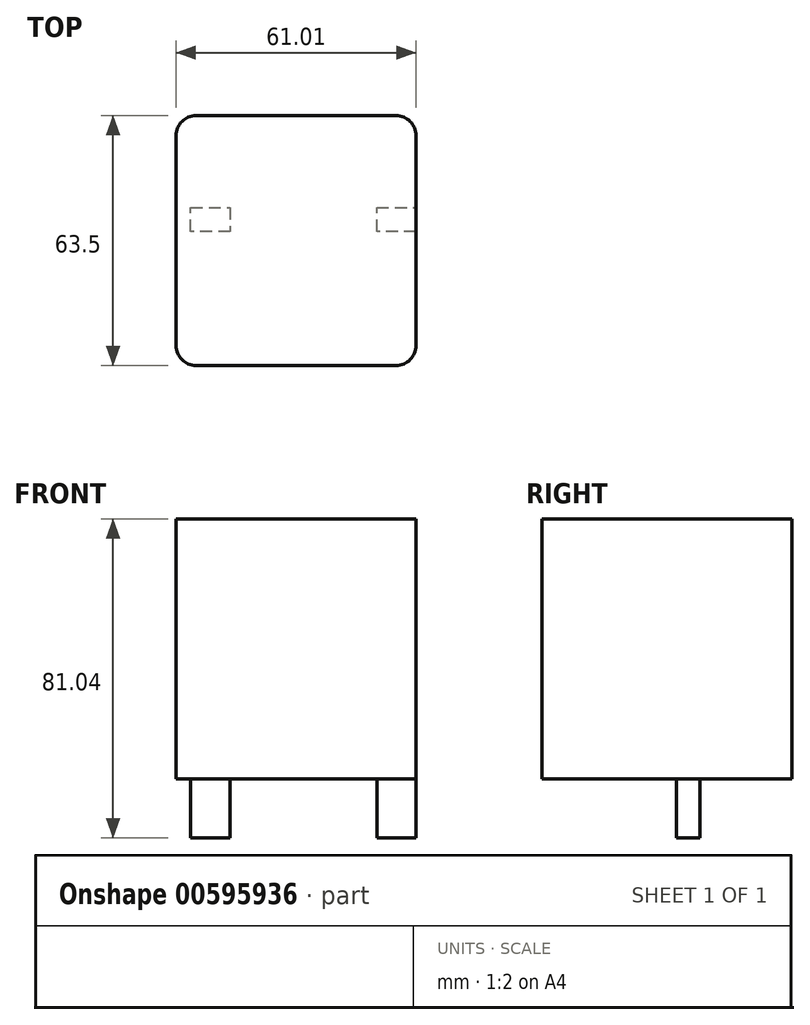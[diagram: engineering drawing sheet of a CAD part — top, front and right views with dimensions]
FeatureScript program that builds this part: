
annotation { "Feature Type Name" : "Feature", "Feature Type Description" : "" }
export const myFeature = defineFeature(function(context is Context, id is Id, definition is map)
    precondition{}
    {
        {
            var Q0;
            Q0=qCreatedBy(makeId("Right.planeOp"),FACE);
            var sketch = newSketch(context, id + "F0", { "sketchPlane" : qUnion([Q0])});
            skLineSegment(sketch, "E0", {"start": v(-37.4, 48.63) * mm, "end": v(26.1, 48.63) * mm});
            skLineSegment(sketch, "E1", {"start": v(26.1, 48.63) * mm, "end": v(26.1, -17.4) * mm});
            skLineSegment(sketch, "E2", {"start": v(26.1, -17.4) * mm, "end": v(-37.4, -17.4) * mm});
            skLineSegment(sketch, "E3", {"start": v(-37.4, -17.4) * mm, "end": v(-37.4, 48.63) * mm});
            skSolve(sketch);
        }
        {
            var Q0;
            Q0 = qSketchRegion(id + "F0", true);
            extrude(context, id + "F1", {"entities" : qUnion([Q0]), "depth" : 60.96 * mm, "offsetDistance" : 25.4 * mm});
        }
        {
            var Q0;
            Q0=makeQuery(id+"F1.opExtrude","CAP_EDGE",EDGE,{"disambiguationData":[OSD([sQuery(id+"F0.wireOp",EDGE,"E3")])],"isStart":false});
            var Q1;
            Q1=makeQuery(id+"F1.opExtrude","CAP_EDGE",EDGE,{"disambiguationData":[OSD([sQuery(id+"F0.wireOp",EDGE,"E1")])],"isStart":false});
            var Q2;
            Q2=makeQuery(id+"F1.opExtrude","CAP_EDGE",EDGE,{"disambiguationData":[OSD([sQuery(id+"F0.wireOp",EDGE,"E3")])],"isStart":true});
            var Q3;
            Q3=makeQuery(id+"F1.opExtrude","CAP_EDGE",EDGE,{"disambiguationData":[OSD([sQuery(id+"F0.wireOp",EDGE,"E1")])],"isStart":true});
            fillet(context, id + "F2", {"entities" : qUnion([Q0, Q1, Q2, Q3]), "radius" : 5.08 * mm, "tangentPropagation" : true, "allowEdgeOverflow" : false});
        }
        {
            var Q0;
            Q0=makeQuery(id+"F1.opExtrude","SWEPT_FACE",FACE,{"disambiguationData":[OSD([sQuery(id+"F0.wireOp",EDGE,"E2")])]});
            var sketch = newSketch(context, id + "F3", { "sketchPlane" : qUnion([Q0])});
            skLineSegment(sketch, "E4", {"start": v(30.48, 37.4) * mm, "end": v(30.48, -26.1) * mm, "construction": true});
            skLineSegment(sketch, "E5", {"start": v(0, 5.65) * mm, "end": v(60.96, 5.65) * mm, "construction": true});
            skPoint(sketch, "E6", {"position": v(30.48, 5.65) * mm});
            skLineSegment(sketch, "E7", {"start": v(3.74, 3.31) * mm, "end": v(3.74, -2.69) * mm});
            skLineSegment(sketch, "E8", {"start": v(3.74, -2.69) * mm, "end": v(13.74, -2.69) * mm});
            skLineSegment(sketch, "E9", {"start": v(13.74, -2.69) * mm, "end": v(13.74, 3.31) * mm});
            skLineSegment(sketch, "E10", {"start": v(13.74, 3.31) * mm, "end": v(3.74, 3.31) * mm});
            skLineSegment(sketch, "E11", {"start": v(51, 3.31) * mm, "end": v(51, -2.69) * mm});
            skLineSegment(sketch, "E12", {"start": v(51, -2.69) * mm, "end": v(61, -2.69) * mm});
            skLineSegment(sketch, "E13", {"start": v(61, -2.69) * mm, "end": v(61, 3.31) * mm});
            skLineSegment(sketch, "E14", {"start": v(61, 3.31) * mm, "end": v(51, 3.31) * mm});
            skSolve(sketch);
        }
        {
            var Q0;
            Q0 = qSketchRegion(id + "F3", true);
            extrude(context, id + "F4", {"entities" : qUnion([Q0]), "operationType" : NewBodyOperationType.ADD, "depth" : 15 * mm, "offsetDistance" : 25 * mm});
        }
    });
